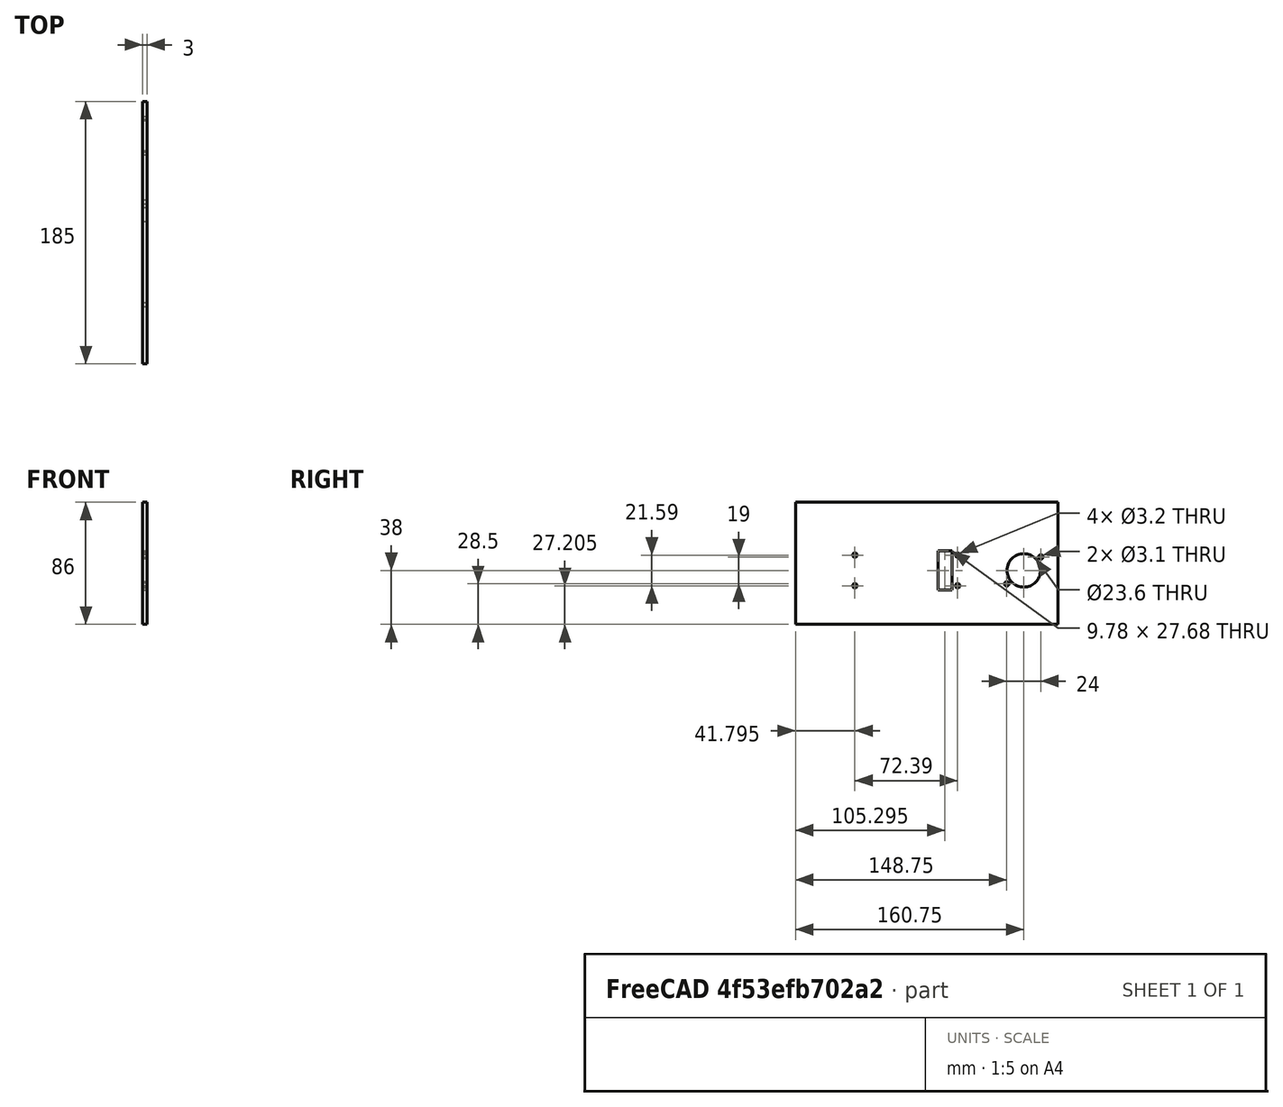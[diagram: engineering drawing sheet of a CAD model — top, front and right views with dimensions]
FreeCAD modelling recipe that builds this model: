
FCSTD DOCUMENT  (FreeCAD 0.20R29410 (Git))
Label: case-top-panel
License: All rights reserved
LicenseURL: http://en.wikipedia.org/wiki/All_rights_reserved
objects: Sketcher::SketchObject×1, PartDesign::Pad×1, PartDesign::Body×1
note: 4 computed .brp shape members not serialized (recipe doc carries the construction recipe); baked Part::Feature solids carry a one-line shape summary decoded from their .brp

FEATURE [Sketcher::SketchObject] Sketch  label="skBase"
  FullyConstrained = true
  MapMode = 5
  Placement = pos=(0,0,0) rot=(0.57735,0.57735,0.57735;2.0944rad)
  Support = -> [YZ_Plane]
  sketch-geometry (28):
    g0: LineSegment StartX=-92.5 StartY=43 StartZ=0 EndX=92.5 EndY=43 EndZ=0
    g1: LineSegment StartX=92.5 StartY=43 StartZ=0 EndX=92.5 EndY=-43 EndZ=0
    g2: LineSegment StartX=92.5 StartY=-43 StartZ=0 EndX=-92.5 EndY=-43 EndZ=0
    g3: LineSegment StartX=-92.5 StartY=-43 StartZ=0 EndX=-92.5 EndY=43 EndZ=0
    g4: Circle CenterX=68.2497 CenterY=-5 CenterZ=0 NormalX=0 NormalY=0 NormalZ=1 AngleXU=0 Radius=11.8
    g5: Circle CenterX=80.2497 CenterY=4.5 CenterZ=0 NormalX=0 NormalY=0 NormalZ=1 AngleXU=0 Radius=1.55
    g6: Circle CenterX=56.2497 CenterY=-14.5 CenterZ=0 NormalX=0 NormalY=0 NormalZ=1 AngleXU=0 Radius=1.55
    g7: LineSegment StartX=-75.4703 StartY=9.605 StartZ=0 EndX=46.4497 EndY=9.605 EndZ=0
    g8: LineSegment StartX=46.4497 StartY=9.605 StartZ=0 EndX=46.4497 EndY=-19.605 EndZ=0
    g9: LineSegment StartX=46.4497 StartY=-19.605 StartZ=0 EndX=-75.4703 EndY=-19.605 EndZ=0
    g10: LineSegment StartX=-75.4703 StartY=-19.605 StartZ=0 EndX=-75.4703 EndY=9.605 EndZ=0
    g11: Circle CenterX=21.6847 CenterY=5.795 CenterZ=0 NormalX=0 NormalY=0 NormalZ=1 AngleXU=0 Radius=1.6
    g12: Circle CenterX=21.6847 CenterY=-15.795 CenterZ=0 NormalX=0 NormalY=0 NormalZ=1 AngleXU=0 Radius=1.6
    g13: Circle CenterX=-50.7053 CenterY=5.795 CenterZ=0 NormalX=0 NormalY=0 NormalZ=1 AngleXU=0 Radius=1.6
    g14: Circle CenterX=-50.7053 CenterY=-15.795 CenterZ=0 NormalX=0 NormalY=0 NormalZ=1 AngleXU=0 Radius=1.6
    g15: LineSegment StartX=-50.7053 StartY=5.795 StartZ=0 EndX=21.6847 EndY=5.795 EndZ=0
    g16: LineSegment StartX=21.6847 StartY=5.795 StartZ=0 EndX=21.6847 EndY=-15.795 EndZ=0
    g17: LineSegment StartX=21.6847 StartY=-15.795 StartZ=0 EndX=-50.7053 EndY=-15.795 EndZ=0
    g18: LineSegment StartX=-50.7053 StartY=-15.795 StartZ=0 EndX=-50.7053 EndY=5.795 EndZ=0
    g19: LineSegment StartX=7.9047 StartY=8.84 StartZ=0 EndX=17.6847 EndY=8.84 EndZ=0
    g20: LineSegment StartX=17.6847 StartY=8.84 StartZ=0 EndX=17.6847 EndY=-18.84 EndZ=0
    g21: LineSegment StartX=17.6847 StartY=-18.84 StartZ=0 EndX=7.9047 EndY=-18.84 EndZ=0
    g22: LineSegment StartX=7.9047 StartY=-18.84 StartZ=0 EndX=7.9047 EndY=8.84 EndZ=0
    g23: LineSegment StartX=46.4497 StartY=9.605 StartZ=0 EndX=-75.4703 EndY=-19.605 EndZ=0
    g24: LineSegment StartX=-75.4703 StartY=9.605 StartZ=0 EndX=46.4497 EndY=-19.605 EndZ=0
    g25: GeomPoint X=-14.5103 Y=-5 Z=0
    g26: LineSegment StartX=-14.5103 StartY=-5 StartZ=0 EndX=68.2497 EndY=-5 EndZ=0
    g27: LineSegment StartX=46.4497 StartY=-5 StartZ=0 EndX=56.4497 EndY=-5 EndZ=0
  constraints (72):
    c: Coincident(g0,g1)
    c: Coincident(g2,g3)
    c: Coincident(g3,g0)
    c: Horizontal(g2)
    c: Vertical(g3)
    c: Distance(g1) = 86
    c: Coincident(g2,g1)
    c: Symmetric(g0,g0,g-2)
    c: Distance(g0) = 185
    c: Symmetric(g0,g1,g-1)
    c: Symmetric(g6,g5,g4)
    c: DistanceY(g6,g5) = 19
    c: DistanceX(g6,g5) = 24
    c: Diameter(g4) = 23.6
    c: Equal(g5,g6)
    c: Diameter(g5) = 3.1
    c: Distance(g4,g1) = 24.2503
    c: Coincident(g7,g8)
    c: Coincident(g8,g9)
    c: Coincident(g9,g10)
    c: Coincident(g10,g7)
    c: Horizontal(g7)
    c: Horizontal(g9)
    c: Vertical(g8)
    c: Vertical(g10)
    c: Distance(g7) = 121.92
    c: Distance(g10) = 29.21
    c: Coincident(g15,g16)
    c: Coincident(g16,g17)
    c: Coincident(g17,g18)
    c: Coincident(g18,g15)
    c: Horizontal(g15)
    c: Horizontal(g17)
    c: Vertical(g16)
    c: Vertical(g18)
    c: Coincident(g15,g13)
    c: Coincident(g16,g12)
    c: Coincident(g11,g15)
    c: Coincident(g14,g17)
    c: Distance(g18) = 21.59
    c: Distance(g17) = 72.39
    c: Coincident(g19,g20)
    c: Coincident(g20,g21)
    c: Coincident(g21,g22)
    c: Coincident(g22,g19)
    c: Horizontal(g19)
    c: Horizontal(g21)
    c: Vertical(g22)
    c: Distance(g20) = 27.68
    c: Distance(g19) = 9.78
    c: Distance(g19,g8) = 28.765
    c: Distance(g13,g10) = 24.765
    c: Coincident(g23,g7)
    c: Coincident(g23,g9)
    c: Coincident(g24,g7)
    c: Coincident(g24,g8)
    c: PointOnObject(g25,g24)
    c: PointOnObject(g25,g23)
    c: Coincident(g26,g25)
    c: Symmetric(g11,g12,g26)
    c: Symmetric(g19,g20,g26)
    c: Equal(g13,g14)
    c: Equal(g13,g12)
    c: Equal(g13,g11)
    c: Diameter(g13) = 3.2
    c: Coincident(g4,g26)
    c: DistanceY(g-1,g4) = -5
    c: PointOnObject(g27,g8)
    c: PointOnObject(g27,g4)
    c: PointOnObject(g27,g26)
    c: Distance(g27) = 10
    c: PointOnObject(g27,g26)
FEATURE [PartDesign::Pad] Pad  label="pdBase"
  Direction = (1,-2e-16,3e-16)
  Length = 3
  Length2 = 10
  Placement = pos=(0,0,0) rot=(0.57735,0.57735,0.57735;2.0944rad)
  Profile = -> Sketch
  ReferenceAxis = -> Sketch [N_Axis]
  Type = 0
FEATURE [PartDesign::Body] Body
  Group = -> [Sketch,Pad]
  Origin = -> Origin
  Tip = -> Pad
